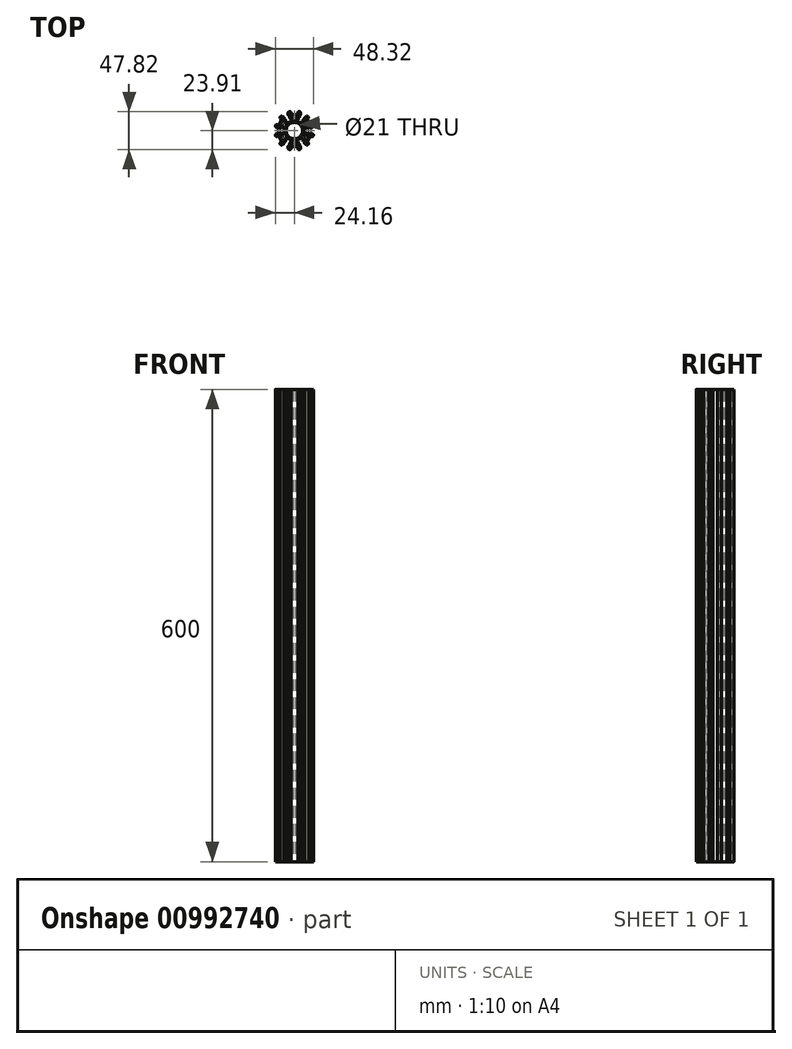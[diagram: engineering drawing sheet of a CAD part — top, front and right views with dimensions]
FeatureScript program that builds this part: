
annotation { "Feature Type Name" : "Feature", "Feature Type Description" : "" }
export const myFeature = defineFeature(function(context is Context, id is Id, definition is map)
    precondition{}
    {
        {
            var Q0;
            Q0=qCreatedBy(makeId("Top.planeOp"),FACE);
            var sketch = newSketch(context, id + "F0", { "sketchPlane" : qUnion([Q0])});
            skLineSegment(sketch, "E0.bottom", {"start": v(-8, -23.9) * mm, "end": v(-4.5, -23.9) * mm});
            skLineSegment(sketch, "E0.top", {"start": v(-8, -19.1) * mm, "end": v(-1.5, -19.1) * mm});
            skLineSegment(sketch, "E0.left", {"start": v(-8, -23.9) * mm, "end": v(-8, -19.1) * mm});
            skLineSegment(sketch, "E0.right", {"start": v(8, -23.9) * mm, "end": v(8, -19.1) * mm});
            skLineSegment(sketch, "E1.bottom", {"start": v(-6.25, -22.6) * mm, "end": v(-4.5, -22.6) * mm});
            skLineSegment(sketch, "E1.top", {"start": v(-6.25, -20.6) * mm, "end": v(6.25, -20.6) * mm});
            skLineSegment(sketch, "E1.left", {"start": v(-6.25, -22.6) * mm, "end": v(-6.25, -20.6) * mm});
            skLineSegment(sketch, "E1.right", {"start": v(6.25, -22.6) * mm, "end": v(6.25, -20.6) * mm});
            skLineSegment(sketch, "E2.left", {"start": v(-1.5, -19.1) * mm, "end": v(-1.5, -17.7) * mm});
            skLineSegment(sketch, "E2.right", {"start": v(1.5, -19.1) * mm, "end": v(1.5, -17.7) * mm});
            skArc(sketch, "E3", {"start": v(1.5, -12.4) * mm, "mid": v(6.25, -10.83) * mm, "end": v(10, -7.5) * mm});
            skLineSegment(sketch, "E4.left", {"start": v(-4.5, -23.9) * mm, "end": v(-4.5, -22.6) * mm});
            skLineSegment(sketch, "E4.right", {"start": v(4.5, -23.9) * mm, "end": v(4.5, -22.6) * mm});
            skLineSegment(sketch, "E5.trimOffspring", {"start": v(4.5, -23.9) * mm, "end": v(8, -23.9) * mm});
            skLineSegment(sketch, "E6.trimOffspring", {"start": v(4.5, -22.6) * mm, "end": v(6.25, -22.6) * mm});
            skLineSegment(sketch, "E7.trimOffspring", {"start": v(1.5, -19.1) * mm, "end": v(8, -19.1) * mm});
            skCircle(sketch, "E8", {"center": v(0, 0) * mm, "radius": 10.5 * mm});
            skLineSegment(sketch, "E9.bottom", {"start": v(-6.5, -17.7) * mm, "end": v(-1.5, -17.7) * mm});
            skLineSegment(sketch, "E9.top", {"start": v(-6.5, -16.4) * mm, "end": v(-1.5, -16.4) * mm});
            skLineSegment(sketch, "E9.left", {"start": v(-6.5, -17.7) * mm, "end": v(-6.5, -16.4) * mm});
            skLineSegment(sketch, "E9.right", {"start": v(6.5, -17.7) * mm, "end": v(6.5, -16.4) * mm});
            skLineSegment(sketch, "E10.bottom", {"start": v(-5, -15) * mm, "end": v(-1.5, -15) * mm});
            skLineSegment(sketch, "E10.top", {"start": v(-5, -13.7) * mm, "end": v(-1.5, -13.7) * mm});
            skLineSegment(sketch, "E10.left", {"start": v(-5, -15) * mm, "end": v(-5, -13.7) * mm});
            skLineSegment(sketch, "E10.right", {"start": v(5, -15) * mm, "end": v(5, -13.7) * mm});
            skLineSegment(sketch, "E11.trimOffspring", {"start": v(1.5, -17.7) * mm, "end": v(6.5, -17.7) * mm});
            skLineSegment(sketch, "E12.trimOffspring", {"start": v(-1.5, -16.4) * mm, "end": v(-1.5, -15) * mm});
            skLineSegment(sketch, "E13.trimOffspring", {"start": v(1.5, -16.4) * mm, "end": v(6.5, -16.4) * mm});
            skLineSegment(sketch, "E14.trimOffspring", {"start": v(1.5, -15) * mm, "end": v(5, -15) * mm});
            skLineSegment(sketch, "E15.trimOffspring", {"start": v(1.5, -16.4) * mm, "end": v(1.5, -15) * mm});
            skLineSegment(sketch, "E16.trimOffspring", {"start": v(1.5, -13.7) * mm, "end": v(1.5, -12.4) * mm});
            skLineSegment(sketch, "E17.trimOffspring", {"start": v(-1.5, -13.7) * mm, "end": v(-1.5, -12.4) * mm});
            skLineSegment(sketch, "E18.trimOffspring", {"start": v(1.5, -13.7) * mm, "end": v(5, -13.7) * mm});
            skLineSegment(sketch, "E19.1.0", {"start": v(16.7, -18.88) * mm, "end": v(18.46, -15.85) * mm});
            skLineSegment(sketch, "E19.1.1", {"start": v(13.75, -6.2) * mm, "end": v(15.5, -3.17) * mm});
            skLineSegment(sketch, "E19.1.2", {"start": v(12.55, -16.48) * mm, "end": v(15.8, -10.85) * mm});
            skLineSegment(sketch, "E19.1.3", {"start": v(24.7, -5.03) * mm, "end": v(20.55, -2.63) * mm});
            skLineSegment(sketch, "E19.1.4", {"start": v(10.5, -11.83) * mm, "end": v(12.25, -8.8) * mm});
            skLineSegment(sketch, "E19.1.5", {"start": v(9.37, -11.18) * mm, "end": v(11.12, -8.15) * mm});
            skLineSegment(sketch, "E19.1.6", {"start": v(16.46, -16.72) * mm, "end": v(14.72, -15.72) * mm});
            skLineSegment(sketch, "E19.1.7", {"start": v(14.96, -6.9) * mm, "end": v(17.46, -2.58) * mm});
            skLineSegment(sketch, "E19.1.8", {"start": v(12.62, -5.56) * mm, "end": v(14.37, -2.52) * mm});
            skLineSegment(sketch, "E19.1.9", {"start": v(22.96, -8.06) * mm, "end": v(24.7, -5.03) * mm});
            skLineSegment(sketch, "E19.1.10", {"start": v(14.72, -15.72) * mm, "end": v(20.97, -4.9) * mm});
            skLineSegment(sketch, "E19.1.11", {"start": v(22.7, -5.9) * mm, "end": v(20.97, -4.9) * mm});
            skLineSegment(sketch, "E19.1.12", {"start": v(16.7, -18.88) * mm, "end": v(12.55, -16.48) * mm});
            skLineSegment(sketch, "E19.1.13", {"start": v(17.3, -8.26) * mm, "end": v(20.55, -2.63) * mm});
            skLineSegment(sketch, "E19.1.14", {"start": v(12.09, -14.48) * mm, "end": v(14.59, -10.15) * mm});
            skLineSegment(sketch, "E19.1.15", {"start": v(10.96, -13.83) * mm, "end": v(13.46, -9.5) * mm});
            skLineSegment(sketch, "E19.1.16", {"start": v(16.09, -7.56) * mm, "end": v(18.59, -3.23) * mm});
            skLineSegment(sketch, "E19.1.17", {"start": v(22.96, -8.06) * mm, "end": v(21.83, -7.4) * mm});
            skLineSegment(sketch, "E19.1.18", {"start": v(13.46, -9.5) * mm, "end": v(12.25, -8.8) * mm});
            skLineSegment(sketch, "E19.1.19", {"start": v(15.5, -3.17) * mm, "end": v(14.37, -2.52) * mm});
            skLineSegment(sketch, "E19.1.20", {"start": v(21.83, -7.4) * mm, "end": v(22.7, -5.9) * mm});
            skLineSegment(sketch, "E19.1.21", {"start": v(18.46, -15.85) * mm, "end": v(17.33, -15.2) * mm});
            skLineSegment(sketch, "E19.1.22", {"start": v(10.5, -11.83) * mm, "end": v(9.37, -11.18) * mm});
            skLineSegment(sketch, "E19.1.23", {"start": v(12.09, -14.48) * mm, "end": v(10.96, -13.83) * mm});
            skLineSegment(sketch, "E19.1.24", {"start": v(15.8, -10.85) * mm, "end": v(14.59, -10.15) * mm});
            skLineSegment(sketch, "E19.1.25", {"start": v(17.3, -8.26) * mm, "end": v(16.09, -7.56) * mm});
            skLineSegment(sketch, "E19.1.26", {"start": v(16.46, -16.72) * mm, "end": v(17.33, -15.2) * mm});
            skLineSegment(sketch, "E19.1.27", {"start": v(18.59, -3.23) * mm, "end": v(17.46, -2.58) * mm});
            skLineSegment(sketch, "E19.1.28", {"start": v(14.96, -6.9) * mm, "end": v(13.75, -6.2) * mm});
            skLineSegment(sketch, "E19.1.29", {"start": v(11.12, -8.15) * mm, "end": v(10, -7.5) * mm});
            skLineSegment(sketch, "E19.1.30", {"start": v(12.62, -5.56) * mm, "end": v(11.5, -4.9) * mm});
            skLineSegment(sketch, "E19.2.0", {"start": v(24.7, 5.03) * mm, "end": v(22.96, 8.06) * mm});
            skLineSegment(sketch, "E19.2.1", {"start": v(12.25, 8.8) * mm, "end": v(10.5, 11.83) * mm});
            skLineSegment(sketch, "E19.2.2", {"start": v(20.55, 2.63) * mm, "end": v(17.3, 8.26) * mm});
            skLineSegment(sketch, "E19.2.3", {"start": v(16.7, 18.88) * mm, "end": v(12.55, 16.48) * mm});
            skLineSegment(sketch, "E19.2.4", {"start": v(15.5, 3.17) * mm, "end": v(13.75, 6.2) * mm});
            skLineSegment(sketch, "E19.2.5", {"start": v(14.37, 2.52) * mm, "end": v(12.62, 5.56) * mm});
            skLineSegment(sketch, "E19.2.6", {"start": v(22.7, 5.9) * mm, "end": v(20.97, 4.9) * mm});
            skLineSegment(sketch, "E19.2.7", {"start": v(13.46, 9.5) * mm, "end": v(10.96, 13.83) * mm});
            skLineSegment(sketch, "E19.2.8", {"start": v(11.12, 8.15) * mm, "end": v(9.37, 11.18) * mm});
            skLineSegment(sketch, "E19.2.9", {"start": v(18.46, 15.85) * mm, "end": v(16.7, 18.88) * mm});
            skLineSegment(sketch, "E19.2.10", {"start": v(20.97, 4.9) * mm, "end": v(14.72, 15.72) * mm});
            skLineSegment(sketch, "E19.2.11", {"start": v(16.46, 16.72) * mm, "end": v(14.72, 15.72) * mm});
            skLineSegment(sketch, "E19.2.12", {"start": v(24.7, 5.03) * mm, "end": v(20.55, 2.63) * mm});
            skLineSegment(sketch, "E19.2.13", {"start": v(15.8, 10.85) * mm, "end": v(12.55, 16.48) * mm});
            skLineSegment(sketch, "E19.2.14", {"start": v(18.59, 3.23) * mm, "end": v(16.09, 7.56) * mm});
            skLineSegment(sketch, "E19.2.15", {"start": v(17.46, 2.58) * mm, "end": v(14.96, 6.9) * mm});
            skLineSegment(sketch, "E19.2.16", {"start": v(14.59, 10.15) * mm, "end": v(12.09, 14.48) * mm});
            skLineSegment(sketch, "E19.2.17", {"start": v(18.46, 15.85) * mm, "end": v(17.33, 15.2) * mm});
            skLineSegment(sketch, "E19.2.18", {"start": v(14.96, 6.9) * mm, "end": v(13.75, 6.2) * mm});
            skLineSegment(sketch, "E19.2.19", {"start": v(10.5, 11.83) * mm, "end": v(9.37, 11.18) * mm});
            skLineSegment(sketch, "E19.2.20", {"start": v(17.33, 15.2) * mm, "end": v(16.46, 16.72) * mm});
            skLineSegment(sketch, "E19.2.21", {"start": v(22.96, 8.06) * mm, "end": v(21.83, 7.4) * mm});
            skLineSegment(sketch, "E19.2.22", {"start": v(15.5, 3.17) * mm, "end": v(14.37, 2.52) * mm});
            skLineSegment(sketch, "E19.2.23", {"start": v(18.59, 3.23) * mm, "end": v(17.46, 2.58) * mm});
            skLineSegment(sketch, "E19.2.24", {"start": v(17.3, 8.26) * mm, "end": v(16.09, 7.56) * mm});
            skLineSegment(sketch, "E19.2.25", {"start": v(15.8, 10.85) * mm, "end": v(14.59, 10.15) * mm});
            skLineSegment(sketch, "E19.2.26", {"start": v(22.7, 5.9) * mm, "end": v(21.83, 7.4) * mm});
            skLineSegment(sketch, "E19.2.27", {"start": v(12.09, 14.48) * mm, "end": v(10.96, 13.83) * mm});
            skLineSegment(sketch, "E19.2.28", {"start": v(13.46, 9.5) * mm, "end": v(12.25, 8.8) * mm});
            skLineSegment(sketch, "E19.2.29", {"start": v(12.62, 5.56) * mm, "end": v(11.5, 4.9) * mm});
            skLineSegment(sketch, "E19.2.30", {"start": v(11.12, 8.15) * mm, "end": v(10, 7.5) * mm});
            skLineSegment(sketch, "E19.3.0", {"start": v(8, 23.9) * mm, "end": v(4.5, 23.9) * mm});
            skLineSegment(sketch, "E19.3.1", {"start": v(-1.5, 15) * mm, "end": v(-5, 15) * mm});
            skLineSegment(sketch, "E19.3.2", {"start": v(8, 19.1) * mm, "end": v(1.5, 19.1) * mm});
            skLineSegment(sketch, "E19.3.3", {"start": v(-8, 23.9) * mm, "end": v(-8, 19.1) * mm});
            skLineSegment(sketch, "E19.3.4", {"start": v(5, 15) * mm, "end": v(1.5, 15) * mm});
            skLineSegment(sketch, "E19.3.5", {"start": v(5, 13.7) * mm, "end": v(1.5, 13.7) * mm});
            skLineSegment(sketch, "E19.3.6", {"start": v(6.25, 22.6) * mm, "end": v(6.25, 20.6) * mm});
            skLineSegment(sketch, "E19.3.7", {"start": v(-1.5, 16.4) * mm, "end": v(-6.5, 16.4) * mm});
            skLineSegment(sketch, "E19.3.8", {"start": v(-1.5, 13.7) * mm, "end": v(-5, 13.7) * mm});
            skLineSegment(sketch, "E19.3.9", {"start": v(-4.5, 23.9) * mm, "end": v(-8, 23.9) * mm});
            skLineSegment(sketch, "E19.3.10", {"start": v(6.25, 20.6) * mm, "end": v(-6.25, 20.6) * mm});
            skLineSegment(sketch, "E19.3.11", {"start": v(-6.25, 22.6) * mm, "end": v(-6.25, 20.6) * mm});
            skLineSegment(sketch, "E19.3.12", {"start": v(8, 23.9) * mm, "end": v(8, 19.1) * mm});
            skLineSegment(sketch, "E19.3.13", {"start": v(-1.5, 19.1) * mm, "end": v(-8, 19.1) * mm});
            skLineSegment(sketch, "E19.3.14", {"start": v(6.5, 17.7) * mm, "end": v(1.5, 17.7) * mm});
            skLineSegment(sketch, "E19.3.15", {"start": v(6.5, 16.4) * mm, "end": v(1.5, 16.4) * mm});
            skLineSegment(sketch, "E19.3.16", {"start": v(-1.5, 17.7) * mm, "end": v(-6.5, 17.7) * mm});
            skLineSegment(sketch, "E19.3.17", {"start": v(-4.5, 23.9) * mm, "end": v(-4.5, 22.6) * mm});
            skLineSegment(sketch, "E19.3.18", {"start": v(1.5, 16.4) * mm, "end": v(1.5, 15) * mm});
            skLineSegment(sketch, "E19.3.19", {"start": v(-5, 15) * mm, "end": v(-5, 13.7) * mm});
            skLineSegment(sketch, "E19.3.20", {"start": v(-4.5, 22.6) * mm, "end": v(-6.25, 22.6) * mm});
            skLineSegment(sketch, "E19.3.21", {"start": v(4.5, 23.9) * mm, "end": v(4.5, 22.6) * mm});
            skLineSegment(sketch, "E19.3.22", {"start": v(5, 15) * mm, "end": v(5, 13.7) * mm});
            skLineSegment(sketch, "E19.3.23", {"start": v(6.5, 17.7) * mm, "end": v(6.5, 16.4) * mm});
            skLineSegment(sketch, "E19.3.24", {"start": v(1.5, 19.1) * mm, "end": v(1.5, 17.7) * mm});
            skLineSegment(sketch, "E19.3.25", {"start": v(-1.5, 19.1) * mm, "end": v(-1.5, 17.7) * mm});
            skLineSegment(sketch, "E19.3.26", {"start": v(6.25, 22.6) * mm, "end": v(4.5, 22.6) * mm});
            skLineSegment(sketch, "E19.3.27", {"start": v(-6.5, 17.7) * mm, "end": v(-6.5, 16.4) * mm});
            skLineSegment(sketch, "E19.3.28", {"start": v(-1.5, 16.4) * mm, "end": v(-1.5, 15) * mm});
            skLineSegment(sketch, "E19.3.29", {"start": v(1.5, 13.7) * mm, "end": v(1.5, 12.4) * mm});
            skLineSegment(sketch, "E19.3.30", {"start": v(-1.5, 13.7) * mm, "end": v(-1.5, 12.4) * mm});
            skLineSegment(sketch, "E19.4.0", {"start": v(-16.7, 18.88) * mm, "end": v(-18.46, 15.85) * mm});
            skLineSegment(sketch, "E19.4.1", {"start": v(-13.75, 6.2) * mm, "end": v(-15.5, 3.17) * mm});
            skLineSegment(sketch, "E19.4.2", {"start": v(-12.55, 16.48) * mm, "end": v(-15.8, 10.85) * mm});
            skLineSegment(sketch, "E19.4.3", {"start": v(-24.7, 5.03) * mm, "end": v(-20.55, 2.63) * mm});
            skLineSegment(sketch, "E19.4.4", {"start": v(-10.5, 11.83) * mm, "end": v(-12.25, 8.8) * mm});
            skLineSegment(sketch, "E19.4.5", {"start": v(-9.37, 11.18) * mm, "end": v(-11.12, 8.15) * mm});
            skLineSegment(sketch, "E19.4.6", {"start": v(-16.46, 16.72) * mm, "end": v(-14.72, 15.72) * mm});
            skLineSegment(sketch, "E19.4.7", {"start": v(-14.96, 6.9) * mm, "end": v(-17.46, 2.58) * mm});
            skLineSegment(sketch, "E19.4.8", {"start": v(-12.62, 5.56) * mm, "end": v(-14.37, 2.52) * mm});
            skLineSegment(sketch, "E19.4.9", {"start": v(-22.96, 8.06) * mm, "end": v(-24.7, 5.03) * mm});
            skLineSegment(sketch, "E19.4.10", {"start": v(-14.72, 15.72) * mm, "end": v(-20.97, 4.9) * mm});
            skLineSegment(sketch, "E19.4.11", {"start": v(-22.7, 5.9) * mm, "end": v(-20.97, 4.9) * mm});
            skLineSegment(sketch, "E19.4.12", {"start": v(-16.7, 18.88) * mm, "end": v(-12.55, 16.48) * mm});
            skLineSegment(sketch, "E19.4.13", {"start": v(-17.3, 8.26) * mm, "end": v(-20.55, 2.63) * mm});
            skLineSegment(sketch, "E19.4.14", {"start": v(-12.09, 14.48) * mm, "end": v(-14.59, 10.15) * mm});
            skLineSegment(sketch, "E19.4.15", {"start": v(-10.96, 13.83) * mm, "end": v(-13.46, 9.5) * mm});
            skLineSegment(sketch, "E19.4.16", {"start": v(-16.09, 7.56) * mm, "end": v(-18.59, 3.23) * mm});
            skLineSegment(sketch, "E19.4.17", {"start": v(-22.96, 8.06) * mm, "end": v(-21.83, 7.4) * mm});
            skLineSegment(sketch, "E19.4.18", {"start": v(-13.46, 9.5) * mm, "end": v(-12.25, 8.8) * mm});
            skLineSegment(sketch, "E19.4.19", {"start": v(-15.5, 3.17) * mm, "end": v(-14.37, 2.52) * mm});
            skLineSegment(sketch, "E19.4.20", {"start": v(-21.83, 7.4) * mm, "end": v(-22.7, 5.9) * mm});
            skLineSegment(sketch, "E19.4.21", {"start": v(-18.46, 15.85) * mm, "end": v(-17.33, 15.2) * mm});
            skLineSegment(sketch, "E19.4.22", {"start": v(-10.5, 11.83) * mm, "end": v(-9.37, 11.18) * mm});
            skLineSegment(sketch, "E19.4.23", {"start": v(-12.09, 14.48) * mm, "end": v(-10.96, 13.83) * mm});
            skLineSegment(sketch, "E19.4.24", {"start": v(-15.8, 10.85) * mm, "end": v(-14.59, 10.15) * mm});
            skLineSegment(sketch, "E19.4.25", {"start": v(-17.3, 8.26) * mm, "end": v(-16.09, 7.56) * mm});
            skLineSegment(sketch, "E19.4.26", {"start": v(-16.46, 16.72) * mm, "end": v(-17.33, 15.2) * mm});
            skLineSegment(sketch, "E19.4.27", {"start": v(-18.59, 3.23) * mm, "end": v(-17.46, 2.58) * mm});
            skLineSegment(sketch, "E19.4.28", {"start": v(-14.96, 6.9) * mm, "end": v(-13.75, 6.2) * mm});
            skLineSegment(sketch, "E19.4.29", {"start": v(-11.12, 8.15) * mm, "end": v(-10, 7.5) * mm});
            skLineSegment(sketch, "E19.4.30", {"start": v(-12.62, 5.56) * mm, "end": v(-11.5, 4.9) * mm});
            skLineSegment(sketch, "E19.5.0", {"start": v(-24.7, -5.03) * mm, "end": v(-22.96, -8.06) * mm});
            skLineSegment(sketch, "E19.5.1", {"start": v(-12.25, -8.8) * mm, "end": v(-10.5, -11.83) * mm});
            skLineSegment(sketch, "E19.5.2", {"start": v(-20.55, -2.63) * mm, "end": v(-17.3, -8.26) * mm});
            skLineSegment(sketch, "E19.5.3", {"start": v(-16.7, -18.88) * mm, "end": v(-12.55, -16.48) * mm});
            skLineSegment(sketch, "E19.5.4", {"start": v(-15.5, -3.17) * mm, "end": v(-13.75, -6.2) * mm});
            skLineSegment(sketch, "E19.5.5", {"start": v(-14.37, -2.52) * mm, "end": v(-12.62, -5.56) * mm});
            skLineSegment(sketch, "E19.5.6", {"start": v(-22.7, -5.9) * mm, "end": v(-20.97, -4.9) * mm});
            skLineSegment(sketch, "E19.5.7", {"start": v(-13.46, -9.5) * mm, "end": v(-10.96, -13.83) * mm});
            skLineSegment(sketch, "E19.5.8", {"start": v(-11.12, -8.15) * mm, "end": v(-9.37, -11.18) * mm});
            skLineSegment(sketch, "E19.5.9", {"start": v(-18.46, -15.85) * mm, "end": v(-16.7, -18.88) * mm});
            skLineSegment(sketch, "E19.5.10", {"start": v(-20.97, -4.9) * mm, "end": v(-14.72, -15.72) * mm});
            skLineSegment(sketch, "E19.5.11", {"start": v(-16.46, -16.72) * mm, "end": v(-14.72, -15.72) * mm});
            skLineSegment(sketch, "E19.5.12", {"start": v(-24.7, -5.03) * mm, "end": v(-20.55, -2.63) * mm});
            skLineSegment(sketch, "E19.5.13", {"start": v(-15.8, -10.85) * mm, "end": v(-12.55, -16.48) * mm});
            skLineSegment(sketch, "E19.5.14", {"start": v(-18.59, -3.23) * mm, "end": v(-16.09, -7.56) * mm});
            skLineSegment(sketch, "E19.5.15", {"start": v(-17.46, -2.58) * mm, "end": v(-14.96, -6.9) * mm});
            skLineSegment(sketch, "E19.5.16", {"start": v(-14.59, -10.15) * mm, "end": v(-12.09, -14.48) * mm});
            skLineSegment(sketch, "E19.5.17", {"start": v(-18.46, -15.85) * mm, "end": v(-17.33, -15.2) * mm});
            skLineSegment(sketch, "E19.5.18", {"start": v(-14.96, -6.9) * mm, "end": v(-13.75, -6.2) * mm});
            skLineSegment(sketch, "E19.5.19", {"start": v(-10.5, -11.83) * mm, "end": v(-9.37, -11.18) * mm});
            skLineSegment(sketch, "E19.5.20", {"start": v(-17.33, -15.2) * mm, "end": v(-16.46, -16.72) * mm});
            skLineSegment(sketch, "E19.5.21", {"start": v(-22.96, -8.06) * mm, "end": v(-21.83, -7.4) * mm});
            skLineSegment(sketch, "E19.5.22", {"start": v(-15.5, -3.17) * mm, "end": v(-14.37, -2.52) * mm});
            skLineSegment(sketch, "E19.5.23", {"start": v(-18.59, -3.23) * mm, "end": v(-17.46, -2.58) * mm});
            skLineSegment(sketch, "E19.5.24", {"start": v(-17.3, -8.26) * mm, "end": v(-16.09, -7.56) * mm});
            skLineSegment(sketch, "E19.5.25", {"start": v(-15.8, -10.85) * mm, "end": v(-14.59, -10.15) * mm});
            skLineSegment(sketch, "E19.5.26", {"start": v(-22.7, -5.9) * mm, "end": v(-21.83, -7.4) * mm});
            skLineSegment(sketch, "E19.5.27", {"start": v(-12.09, -14.48) * mm, "end": v(-10.96, -13.83) * mm});
            skLineSegment(sketch, "E19.5.28", {"start": v(-13.46, -9.5) * mm, "end": v(-12.25, -8.8) * mm});
            skLineSegment(sketch, "E19.5.29", {"start": v(-12.62, -5.56) * mm, "end": v(-11.5, -4.9) * mm});
            skLineSegment(sketch, "E19.5.30", {"start": v(-11.12, -8.15) * mm, "end": v(-10, -7.5) * mm});
            skArc(sketch, "E20.trimOffspring", {"start": v(-10, -7.5) * mm, "mid": v(-6.25, -10.83) * mm, "end": v(-1.5, -12.4) * mm});
            skArc(sketch, "E21.trimOffspring", {"start": v(-11.5, 4.9) * mm, "mid": v(-12.5, 0) * mm, "end": v(-11.5, -4.9) * mm});
            skArc(sketch, "E22.trimOffspring", {"start": v(11.5, -4.9) * mm, "mid": v(12.5, 0) * mm, "end": v(11.5, 4.9) * mm});
            skArc(sketch, "E23.trimOffspring", {"start": v(-1.5, 12.4) * mm, "mid": v(-6.25, 10.83) * mm, "end": v(-10, 7.5) * mm});
            skArc(sketch, "E24.trimOffspring", {"start": v(10, 7.5) * mm, "mid": v(6.25, 10.83) * mm, "end": v(1.5, 12.4) * mm});
            skSolve(sketch);
        }
        {
            var Q0;
            Q0 = qSketchRegion(id + "F0", true);
            extrude(context, id + "F1", {"entities" : qUnion([Q0]), "depth" : 600 * mm, "offsetDistance" : 25 * mm});
        }
        {
            var Q0;
            Q0=makeQuery(id+"F1.opExtrude","SWEPT_EDGE",EDGE,{"disambiguationData":[OSD([sQuery(id+"F0.wireOp",EDGE,"E19.3.3"),sQuery(id+"F0.wireOp",EDGE,"E19.3.9")])]});
            var Q1;
            Q1=makeQuery(id+"F1.opExtrude","SWEPT_EDGE",EDGE,{"disambiguationData":[OSD([sQuery(id+"F0.wireOp",EDGE,"E19.3.0"),sQuery(id+"F0.wireOp",EDGE,"E19.3.12")])]});
            var Q2;
            Q2=makeQuery(id+"F1.opExtrude","SWEPT_EDGE",EDGE,{"disambiguationData":[OSD([sQuery(id+"F0.wireOp",EDGE,"E19.3.2"),sQuery(id+"F0.wireOp",EDGE,"E19.3.12")])]});
            var Q3;
            Q3=makeQuery(id+"F1.opExtrude","SWEPT_EDGE",EDGE,{"disambiguationData":[OSD([sQuery(id+"F0.wireOp",EDGE,"E19.3.3"),sQuery(id+"F0.wireOp",EDGE,"E19.3.13")])]});
            var Q4;
            Q4=makeQuery(id+"F1.opExtrude","SWEPT_EDGE",EDGE,{"disambiguationData":[OSD([sQuery(id+"F0.wireOp",EDGE,"E19.2.3"),sQuery(id+"F0.wireOp",EDGE,"E19.2.13")])]});
            var Q5;
            Q5=makeQuery(id+"F1.opExtrude","SWEPT_EDGE",EDGE,{"disambiguationData":[OSD([sQuery(id+"F0.wireOp",EDGE,"E19.2.2"),sQuery(id+"F0.wireOp",EDGE,"E19.2.12")])]});
            var Q6;
            Q6=makeQuery(id+"F1.opExtrude","SWEPT_EDGE",EDGE,{"disambiguationData":[OSD([sQuery(id+"F0.wireOp",EDGE,"E19.2.0"),sQuery(id+"F0.wireOp",EDGE,"E19.2.12")])]});
            var Q7;
            Q7=makeQuery(id+"F1.opExtrude","SWEPT_EDGE",EDGE,{"disambiguationData":[OSD([sQuery(id+"F0.wireOp",EDGE,"E19.2.3"),sQuery(id+"F0.wireOp",EDGE,"E19.2.9")])]});
            var Q8;
            Q8=makeQuery(id+"F1.opExtrude","SWEPT_EDGE",EDGE,{"disambiguationData":[OSD([sQuery(id+"F0.wireOp",EDGE,"E19.1.3"),sQuery(id+"F0.wireOp",EDGE,"E19.1.13")])]});
            var Q9;
            Q9=makeQuery(id+"F1.opExtrude","SWEPT_EDGE",EDGE,{"disambiguationData":[OSD([sQuery(id+"F0.wireOp",EDGE,"E19.1.3"),sQuery(id+"F0.wireOp",EDGE,"E19.1.9")])]});
            var Q10;
            Q10=makeQuery(id+"F1.opExtrude","SWEPT_EDGE",EDGE,{"disambiguationData":[OSD([sQuery(id+"F0.wireOp",EDGE,"E19.1.2"),sQuery(id+"F0.wireOp",EDGE,"E19.1.12")])]});
            var Q11;
            Q11=makeQuery(id+"F1.opExtrude","SWEPT_EDGE",EDGE,{"disambiguationData":[OSD([sQuery(id+"F0.wireOp",EDGE,"E19.1.0"),sQuery(id+"F0.wireOp",EDGE,"E19.1.12")])]});
            var Q12;
            Q12=makeQuery(id+"F1.opExtrude","SWEPT_EDGE",EDGE,{"disambiguationData":[OSD([sQuery(id+"F0.wireOp",EDGE,"E0.right"),sQuery(id+"F0.wireOp",EDGE,"E5.trimOffspring")])]});
            var Q13;
            Q13=makeQuery(id+"F1.opExtrude","SWEPT_EDGE",EDGE,{"disambiguationData":[OSD([sQuery(id+"F0.wireOp",EDGE,"E0.right"),sQuery(id+"F0.wireOp",EDGE,"E7.trimOffspring")])]});
            var Q14;
            Q14=makeQuery(id+"F1.opExtrude","SWEPT_EDGE",EDGE,{"disambiguationData":[OSD([sQuery(id+"F0.wireOp",EDGE,"E0.top"),sQuery(id+"F0.wireOp",EDGE,"E0.left")])]});
            var Q15;
            Q15=makeQuery(id+"F1.opExtrude","SWEPT_EDGE",EDGE,{"disambiguationData":[OSD([sQuery(id+"F0.wireOp",EDGE,"E0.bottom"),sQuery(id+"F0.wireOp",EDGE,"E0.left")])]});
            var Q16;
            Q16=makeQuery(id+"F1.opExtrude","SWEPT_EDGE",EDGE,{"disambiguationData":[OSD([sQuery(id+"F0.wireOp",EDGE,"E19.5.3"),sQuery(id+"F0.wireOp",EDGE,"E19.5.13")])]});
            var Q17;
            Q17=makeQuery(id+"F1.opExtrude","SWEPT_EDGE",EDGE,{"disambiguationData":[OSD([sQuery(id+"F0.wireOp",EDGE,"E19.5.3"),sQuery(id+"F0.wireOp",EDGE,"E19.5.9")])]});
            var Q18;
            Q18=makeQuery(id+"F1.opExtrude","SWEPT_EDGE",EDGE,{"disambiguationData":[OSD([sQuery(id+"F0.wireOp",EDGE,"E19.5.2"),sQuery(id+"F0.wireOp",EDGE,"E19.5.12")])]});
            var Q19;
            Q19=makeQuery(id+"F1.opExtrude","SWEPT_EDGE",EDGE,{"disambiguationData":[OSD([sQuery(id+"F0.wireOp",EDGE,"E19.5.0"),sQuery(id+"F0.wireOp",EDGE,"E19.5.12")])]});
            var Q20;
            Q20=makeQuery(id+"F1.opExtrude","SWEPT_EDGE",EDGE,{"disambiguationData":[OSD([sQuery(id+"F0.wireOp",EDGE,"E19.4.3"),sQuery(id+"F0.wireOp",EDGE,"E19.4.13")])]});
            var Q21;
            Q21=makeQuery(id+"F1.opExtrude","SWEPT_EDGE",EDGE,{"disambiguationData":[OSD([sQuery(id+"F0.wireOp",EDGE,"E19.4.3"),sQuery(id+"F0.wireOp",EDGE,"E19.4.9")])]});
            var Q22;
            Q22=makeQuery(id+"F1.opExtrude","SWEPT_EDGE",EDGE,{"disambiguationData":[OSD([sQuery(id+"F0.wireOp",EDGE,"E19.4.2"),sQuery(id+"F0.wireOp",EDGE,"E19.4.12")])]});
            var Q23;
            Q23=makeQuery(id+"F1.opExtrude","SWEPT_EDGE",EDGE,{"disambiguationData":[OSD([sQuery(id+"F0.wireOp",EDGE,"E19.4.0"),sQuery(id+"F0.wireOp",EDGE,"E19.4.12")])]});
            fillet(context, id + "F2", {"entities" : qUnion([Q0, Q1, Q2, Q3, Q4, Q5, Q6, Q7, Q8, Q9, Q10, Q11, Q12, Q13, Q14, Q15, Q16, Q17, Q18, Q19, Q20, Q21, Q22, Q23]), "tangentPropagation" : true, "radius" : 1.5 * mm, "defaultsChanged" : false, "vertexSettings" : [], "allowEdgeOverflow" : false});
        }
        {
            var Q0;
            Q0=makeQuery(id+"F1.opExtrude","SWEPT_EDGE",EDGE,{"disambiguationData":[OSD([sQuery(id+"F0.wireOp",EDGE,"E19.3.0"),sQuery(id+"F0.wireOp",EDGE,"E19.3.21")])]});
            var Q1;
            Q1=makeQuery(id+"F1.opExtrude","SWEPT_EDGE",EDGE,{"disambiguationData":[OSD([sQuery(id+"F0.wireOp",EDGE,"E19.3.9"),sQuery(id+"F0.wireOp",EDGE,"E19.3.17")])]});
            var Q2;
            Q2=makeQuery(id+"F1.opExtrude","SWEPT_EDGE",EDGE,{"disambiguationData":[OSD([sQuery(id+"F0.wireOp",EDGE,"E19.3.16"),sQuery(id+"F0.wireOp",EDGE,"E19.3.27")])]});
            var Q3;
            Q3=makeQuery(id+"F1.opExtrude","SWEPT_EDGE",EDGE,{"disambiguationData":[OSD([sQuery(id+"F0.wireOp",EDGE,"E19.3.7"),sQuery(id+"F0.wireOp",EDGE,"E19.3.27")])]});
            var Q4;
            Q4=makeQuery(id+"F1.opExtrude","SWEPT_EDGE",EDGE,{"disambiguationData":[OSD([sQuery(id+"F0.wireOp",EDGE,"E19.3.1"),sQuery(id+"F0.wireOp",EDGE,"E19.3.19")])]});
            var Q5;
            Q5=makeQuery(id+"F1.opExtrude","SWEPT_EDGE",EDGE,{"disambiguationData":[OSD([sQuery(id+"F0.wireOp",EDGE,"E19.3.8"),sQuery(id+"F0.wireOp",EDGE,"E19.3.19")])]});
            var Q6;
            Q6=makeQuery(id+"F1.opExtrude","SWEPT_EDGE",EDGE,{"disambiguationData":[OSD([sQuery(id+"F0.wireOp",EDGE,"E19.3.14"),sQuery(id+"F0.wireOp",EDGE,"E19.3.23")])]});
            var Q7;
            Q7=makeQuery(id+"F1.opExtrude","SWEPT_EDGE",EDGE,{"disambiguationData":[OSD([sQuery(id+"F0.wireOp",EDGE,"E19.3.15"),sQuery(id+"F0.wireOp",EDGE,"E19.3.23")])]});
            var Q8;
            Q8=makeQuery(id+"F1.opExtrude","SWEPT_EDGE",EDGE,{"disambiguationData":[OSD([sQuery(id+"F0.wireOp",EDGE,"E19.3.4"),sQuery(id+"F0.wireOp",EDGE,"E19.3.22")])]});
            var Q9;
            Q9=makeQuery(id+"F1.opExtrude","SWEPT_EDGE",EDGE,{"disambiguationData":[OSD([sQuery(id+"F0.wireOp",EDGE,"E19.3.5"),sQuery(id+"F0.wireOp",EDGE,"E19.3.22")])]});
            var Q10;
            Q10=makeQuery(id+"F1.opExtrude","SWEPT_EDGE",EDGE,{"disambiguationData":[OSD([sQuery(id+"F0.wireOp",EDGE,"E19.4.0"),sQuery(id+"F0.wireOp",EDGE,"E19.4.21")])]});
            var Q11;
            Q11=makeQuery(id+"F1.opExtrude","SWEPT_EDGE",EDGE,{"disambiguationData":[OSD([sQuery(id+"F0.wireOp",EDGE,"E19.4.9"),sQuery(id+"F0.wireOp",EDGE,"E19.4.17")])]});
            var Q12;
            Q12=makeQuery(id+"F1.opExtrude","SWEPT_EDGE",EDGE,{"disambiguationData":[OSD([sQuery(id+"F0.wireOp",EDGE,"E19.4.16"),sQuery(id+"F0.wireOp",EDGE,"E19.4.27")])]});
            var Q13;
            Q13=makeQuery(id+"F1.opExtrude","SWEPT_EDGE",EDGE,{"disambiguationData":[OSD([sQuery(id+"F0.wireOp",EDGE,"E19.4.7"),sQuery(id+"F0.wireOp",EDGE,"E19.4.27")])]});
            var Q14;
            Q14=makeQuery(id+"F1.opExtrude","SWEPT_EDGE",EDGE,{"disambiguationData":[OSD([sQuery(id+"F0.wireOp",EDGE,"E19.4.1"),sQuery(id+"F0.wireOp",EDGE,"E19.4.19")])]});
            var Q15;
            Q15=makeQuery(id+"F1.opExtrude","SWEPT_EDGE",EDGE,{"disambiguationData":[OSD([sQuery(id+"F0.wireOp",EDGE,"E19.4.8"),sQuery(id+"F0.wireOp",EDGE,"E19.4.19")])]});
            var Q16;
            Q16=makeQuery(id+"F1.opExtrude","SWEPT_EDGE",EDGE,{"disambiguationData":[OSD([sQuery(id+"F0.wireOp",EDGE,"E19.4.4"),sQuery(id+"F0.wireOp",EDGE,"E19.4.22")])]});
            var Q17;
            Q17=makeQuery(id+"F1.opExtrude","SWEPT_EDGE",EDGE,{"disambiguationData":[OSD([sQuery(id+"F0.wireOp",EDGE,"E19.4.14"),sQuery(id+"F0.wireOp",EDGE,"E19.4.23")])]});
            var Q18;
            Q18=makeQuery(id+"F1.opExtrude","SWEPT_EDGE",EDGE,{"disambiguationData":[OSD([sQuery(id+"F0.wireOp",EDGE,"E19.4.15"),sQuery(id+"F0.wireOp",EDGE,"E19.4.23")])]});
            var Q19;
            Q19=makeQuery(id+"F1.opExtrude","SWEPT_EDGE",EDGE,{"disambiguationData":[OSD([sQuery(id+"F0.wireOp",EDGE,"E19.4.5"),sQuery(id+"F0.wireOp",EDGE,"E19.4.22")])]});
            var Q20;
            Q20=makeQuery(id+"F1.opExtrude","SWEPT_EDGE",EDGE,{"disambiguationData":[OSD([sQuery(id+"F0.wireOp",EDGE,"E19.5.0"),sQuery(id+"F0.wireOp",EDGE,"E19.5.21")])]});
            var Q21;
            Q21=makeQuery(id+"F1.opExtrude","SWEPT_EDGE",EDGE,{"disambiguationData":[OSD([sQuery(id+"F0.wireOp",EDGE,"E19.5.14"),sQuery(id+"F0.wireOp",EDGE,"E19.5.23")])]});
            var Q22;
            Q22=makeQuery(id+"F1.opExtrude","SWEPT_EDGE",EDGE,{"disambiguationData":[OSD([sQuery(id+"F0.wireOp",EDGE,"E19.5.15"),sQuery(id+"F0.wireOp",EDGE,"E19.5.23")])]});
            var Q23;
            Q23=makeQuery(id+"F1.opExtrude","SWEPT_EDGE",EDGE,{"disambiguationData":[OSD([sQuery(id+"F0.wireOp",EDGE,"E19.5.4"),sQuery(id+"F0.wireOp",EDGE,"E19.5.22")])]});
            var Q24;
            Q24=makeQuery(id+"F1.opExtrude","SWEPT_EDGE",EDGE,{"disambiguationData":[OSD([sQuery(id+"F0.wireOp",EDGE,"E19.5.5"),sQuery(id+"F0.wireOp",EDGE,"E19.5.22")])]});
            var Q25;
            Q25=makeQuery(id+"F1.opExtrude","SWEPT_EDGE",EDGE,{"disambiguationData":[OSD([sQuery(id+"F0.wireOp",EDGE,"E19.5.1"),sQuery(id+"F0.wireOp",EDGE,"E19.5.19")])]});
            var Q26;
            Q26=makeQuery(id+"F1.opExtrude","SWEPT_EDGE",EDGE,{"disambiguationData":[OSD([sQuery(id+"F0.wireOp",EDGE,"E19.5.8"),sQuery(id+"F0.wireOp",EDGE,"E19.5.19")])]});
            var Q27;
            Q27=makeQuery(id+"F1.opExtrude","SWEPT_EDGE",EDGE,{"disambiguationData":[OSD([sQuery(id+"F0.wireOp",EDGE,"E19.5.7"),sQuery(id+"F0.wireOp",EDGE,"E19.5.27")])]});
            var Q28;
            Q28=makeQuery(id+"F1.opExtrude","SWEPT_EDGE",EDGE,{"disambiguationData":[OSD([sQuery(id+"F0.wireOp",EDGE,"E19.5.16"),sQuery(id+"F0.wireOp",EDGE,"E19.5.27")])]});
            var Q29;
            Q29=makeQuery(id+"F1.opExtrude","SWEPT_EDGE",EDGE,{"disambiguationData":[OSD([sQuery(id+"F0.wireOp",EDGE,"E19.5.9"),sQuery(id+"F0.wireOp",EDGE,"E19.5.17")])]});
            var Q30;
            Q30=makeQuery(id+"F1.opExtrude","SWEPT_EDGE",EDGE,{"disambiguationData":[OSD([sQuery(id+"F0.wireOp",EDGE,"E9.bottom"),sQuery(id+"F0.wireOp",EDGE,"E9.left")])]});
            var Q31;
            Q31=makeQuery(id+"F1.opExtrude","SWEPT_EDGE",EDGE,{"disambiguationData":[OSD([sQuery(id+"F0.wireOp",EDGE,"E9.top"),sQuery(id+"F0.wireOp",EDGE,"E9.left")])]});
            var Q32;
            Q32=makeQuery(id+"F1.opExtrude","SWEPT_EDGE",EDGE,{"disambiguationData":[OSD([sQuery(id+"F0.wireOp",EDGE,"E10.bottom"),sQuery(id+"F0.wireOp",EDGE,"E10.left")])]});
            var Q33;
            Q33=makeQuery(id+"F1.opExtrude","SWEPT_EDGE",EDGE,{"disambiguationData":[OSD([sQuery(id+"F0.wireOp",EDGE,"E10.top"),sQuery(id+"F0.wireOp",EDGE,"E10.left")])]});
            var Q34;
            Q34=makeQuery(id+"F1.opExtrude","SWEPT_EDGE",EDGE,{"disambiguationData":[OSD([sQuery(id+"F0.wireOp",EDGE,"E0.bottom"),sQuery(id+"F0.wireOp",EDGE,"E4.left")])]});
            var Q35;
            Q35=makeQuery(id+"F1.opExtrude","SWEPT_EDGE",EDGE,{"disambiguationData":[OSD([sQuery(id+"F0.wireOp",EDGE,"E4.right"),sQuery(id+"F0.wireOp",EDGE,"E5.trimOffspring")])]});
            var Q36;
            Q36=makeQuery(id+"F1.opExtrude","SWEPT_EDGE",EDGE,{"disambiguationData":[OSD([sQuery(id+"F0.wireOp",EDGE,"E9.right"),sQuery(id+"F0.wireOp",EDGE,"E11.trimOffspring")])]});
            var Q37;
            Q37=makeQuery(id+"F1.opExtrude","SWEPT_EDGE",EDGE,{"disambiguationData":[OSD([sQuery(id+"F0.wireOp",EDGE,"E9.right"),sQuery(id+"F0.wireOp",EDGE,"E13.trimOffspring")])]});
            var Q38;
            Q38=makeQuery(id+"F1.opExtrude","SWEPT_EDGE",EDGE,{"disambiguationData":[OSD([sQuery(id+"F0.wireOp",EDGE,"E10.right"),sQuery(id+"F0.wireOp",EDGE,"E14.trimOffspring")])]});
            var Q39;
            Q39=makeQuery(id+"F1.opExtrude","SWEPT_EDGE",EDGE,{"disambiguationData":[OSD([sQuery(id+"F0.wireOp",EDGE,"E10.right"),sQuery(id+"F0.wireOp",EDGE,"E18.trimOffspring")])]});
            var Q40;
            Q40=makeQuery(id+"F1.opExtrude","SWEPT_EDGE",EDGE,{"disambiguationData":[OSD([sQuery(id+"F0.wireOp",EDGE,"E19.1.14"),sQuery(id+"F0.wireOp",EDGE,"E19.1.23")])]});
            var Q41;
            Q41=makeQuery(id+"F1.opExtrude","SWEPT_EDGE",EDGE,{"disambiguationData":[OSD([sQuery(id+"F0.wireOp",EDGE,"E19.1.15"),sQuery(id+"F0.wireOp",EDGE,"E19.1.23")])]});
            var Q42;
            Q42=makeQuery(id+"F1.opExtrude","SWEPT_EDGE",EDGE,{"disambiguationData":[OSD([sQuery(id+"F0.wireOp",EDGE,"E19.1.5"),sQuery(id+"F0.wireOp",EDGE,"E19.1.22")])]});
            var Q43;
            Q43=makeQuery(id+"F1.opExtrude","SWEPT_EDGE",EDGE,{"disambiguationData":[OSD([sQuery(id+"F0.wireOp",EDGE,"E19.1.4"),sQuery(id+"F0.wireOp",EDGE,"E19.1.22")])]});
            var Q44;
            Q44=makeQuery(id+"F1.opExtrude","SWEPT_EDGE",EDGE,{"disambiguationData":[OSD([sQuery(id+"F0.wireOp",EDGE,"E19.1.0"),sQuery(id+"F0.wireOp",EDGE,"E19.1.21")])]});
            var Q45;
            Q45=makeQuery(id+"F1.opExtrude","SWEPT_EDGE",EDGE,{"disambiguationData":[OSD([sQuery(id+"F0.wireOp",EDGE,"E19.1.9"),sQuery(id+"F0.wireOp",EDGE,"E19.1.17")])]});
            var Q46;
            Q46=makeQuery(id+"F1.opExtrude","SWEPT_EDGE",EDGE,{"disambiguationData":[OSD([sQuery(id+"F0.wireOp",EDGE,"E19.1.16"),sQuery(id+"F0.wireOp",EDGE,"E19.1.27")])]});
            var Q47;
            Q47=makeQuery(id+"F1.opExtrude","SWEPT_EDGE",EDGE,{"disambiguationData":[OSD([sQuery(id+"F0.wireOp",EDGE,"E19.1.1"),sQuery(id+"F0.wireOp",EDGE,"E19.1.19")])]});
            var Q48;
            Q48=makeQuery(id+"F1.opExtrude","SWEPT_EDGE",EDGE,{"disambiguationData":[OSD([sQuery(id+"F0.wireOp",EDGE,"E19.1.7"),sQuery(id+"F0.wireOp",EDGE,"E19.1.27")])]});
            var Q49;
            Q49=makeQuery(id+"F1.opExtrude","SWEPT_EDGE",EDGE,{"disambiguationData":[OSD([sQuery(id+"F0.wireOp",EDGE,"E19.1.8"),sQuery(id+"F0.wireOp",EDGE,"E19.1.19")])]});
            var Q50;
            Q50=makeQuery(id+"F1.opExtrude","SWEPT_EDGE",EDGE,{"disambiguationData":[OSD([sQuery(id+"F0.wireOp",EDGE,"E19.2.15"),sQuery(id+"F0.wireOp",EDGE,"E19.2.23")])]});
            var Q51;
            Q51=makeQuery(id+"F1.opExtrude","SWEPT_EDGE",EDGE,{"disambiguationData":[OSD([sQuery(id+"F0.wireOp",EDGE,"E19.2.14"),sQuery(id+"F0.wireOp",EDGE,"E19.2.23")])]});
            var Q52;
            Q52=makeQuery(id+"F1.opExtrude","SWEPT_EDGE",EDGE,{"disambiguationData":[OSD([sQuery(id+"F0.wireOp",EDGE,"E19.2.4"),sQuery(id+"F0.wireOp",EDGE,"E19.2.22")])]});
            var Q53;
            Q53=makeQuery(id+"F1.opExtrude","SWEPT_EDGE",EDGE,{"disambiguationData":[OSD([sQuery(id+"F0.wireOp",EDGE,"E19.2.5"),sQuery(id+"F0.wireOp",EDGE,"E19.2.22")])]});
            var Q54;
            Q54=makeQuery(id+"F1.opExtrude","SWEPT_EDGE",EDGE,{"disambiguationData":[OSD([sQuery(id+"F0.wireOp",EDGE,"E19.2.8"),sQuery(id+"F0.wireOp",EDGE,"E19.2.19")])]});
            var Q55;
            Q55=makeQuery(id+"F1.opExtrude","SWEPT_EDGE",EDGE,{"disambiguationData":[OSD([sQuery(id+"F0.wireOp",EDGE,"E19.2.7"),sQuery(id+"F0.wireOp",EDGE,"E19.2.27")])]});
            var Q56;
            Q56=makeQuery(id+"F1.opExtrude","SWEPT_EDGE",EDGE,{"disambiguationData":[OSD([sQuery(id+"F0.wireOp",EDGE,"E19.2.9"),sQuery(id+"F0.wireOp",EDGE,"E19.2.17")])]});
            var Q57;
            Q57=makeQuery(id+"F1.opExtrude","SWEPT_EDGE",EDGE,{"disambiguationData":[OSD([sQuery(id+"F0.wireOp",EDGE,"E19.2.0"),sQuery(id+"F0.wireOp",EDGE,"E19.2.21")])]});
            var Q58;
            Q58=makeQuery(id+"F1.opExtrude","SWEPT_EDGE",EDGE,{"disambiguationData":[OSD([sQuery(id+"F0.wireOp",EDGE,"E19.2.16"),sQuery(id+"F0.wireOp",EDGE,"E19.2.27")])]});
            var Q59;
            Q59=makeQuery(id+"F1.opExtrude","SWEPT_EDGE",EDGE,{"disambiguationData":[OSD([sQuery(id+"F0.wireOp",EDGE,"E19.2.1"),sQuery(id+"F0.wireOp",EDGE,"E19.2.19")])]});
            fillet(context, id + "F3", {"entities" : qUnion([Q0, Q1, Q2, Q3, Q4, Q5, Q6, Q7, Q8, Q9, Q10, Q11, Q12, Q13, Q14, Q15, Q16, Q17, Q18, Q19, Q20, Q21, Q22, Q23, Q24, Q25, Q26, Q27, Q28, Q29, Q30, Q31, Q32, Q33, Q34, Q35, Q36, Q37, Q38, Q39, Q40, Q41, Q42, Q43, Q44, Q45, Q46, Q47, Q48, Q49, Q50, Q51, Q52, Q53, Q54, Q55, Q56, Q57, Q58, Q59]), "tangentPropagation" : true, "radius" : .5 * mm, "defaultsChanged" : false, "vertexSettings" : [], "allowEdgeOverflow" : false});
        }
        {
            var Q0;
            Q0=makeQuery(id+"F1.opExtrude","SWEPT_EDGE",EDGE,{"disambiguationData":[OSD([sQuery(id+"F0.wireOp",EDGE,"E19.1.2"),sQuery(id+"F0.wireOp",EDGE,"E19.1.24")])]});
            var Q1;
            Q1=makeQuery(id+"F1.opExtrude","SWEPT_EDGE",EDGE,{"disambiguationData":[OSD([sQuery(id+"F0.wireOp",EDGE,"E19.1.13"),sQuery(id+"F0.wireOp",EDGE,"E19.1.25")])]});
            var Q2;
            Q2=makeQuery(id+"F1.opExtrude","SWEPT_EDGE",EDGE,{"disambiguationData":[OSD([sQuery(id+"F0.wireOp",EDGE,"E0.top"),sQuery(id+"F0.wireOp",EDGE,"E2.left")])]});
            var Q3;
            Q3=makeQuery(id+"F1.opExtrude","SWEPT_EDGE",EDGE,{"disambiguationData":[OSD([sQuery(id+"F0.wireOp",EDGE,"E2.right"),sQuery(id+"F0.wireOp",EDGE,"E7.trimOffspring")])]});
            var Q4;
            Q4=makeQuery(id+"F1.opExtrude","SWEPT_EDGE",EDGE,{"disambiguationData":[OSD([sQuery(id+"F0.wireOp",EDGE,"E19.5.13"),sQuery(id+"F0.wireOp",EDGE,"E19.5.25")])]});
            var Q5;
            Q5=makeQuery(id+"F1.opExtrude","SWEPT_EDGE",EDGE,{"disambiguationData":[OSD([sQuery(id+"F0.wireOp",EDGE,"E19.5.2"),sQuery(id+"F0.wireOp",EDGE,"E19.5.24")])]});
            var Q6;
            Q6=makeQuery(id+"F1.opExtrude","SWEPT_EDGE",EDGE,{"disambiguationData":[OSD([sQuery(id+"F0.wireOp",EDGE,"E19.4.13"),sQuery(id+"F0.wireOp",EDGE,"E19.4.25")])]});
            var Q7;
            Q7=makeQuery(id+"F1.opExtrude","SWEPT_EDGE",EDGE,{"disambiguationData":[OSD([sQuery(id+"F0.wireOp",EDGE,"E19.4.2"),sQuery(id+"F0.wireOp",EDGE,"E19.4.24")])]});
            var Q8;
            Q8=makeQuery(id+"F1.opExtrude","SWEPT_EDGE",EDGE,{"disambiguationData":[OSD([sQuery(id+"F0.wireOp",EDGE,"E19.3.13"),sQuery(id+"F0.wireOp",EDGE,"E19.3.25")])]});
            var Q9;
            Q9=makeQuery(id+"F1.opExtrude","SWEPT_EDGE",EDGE,{"disambiguationData":[OSD([sQuery(id+"F0.wireOp",EDGE,"E19.3.2"),sQuery(id+"F0.wireOp",EDGE,"E19.3.24")])]});
            var Q10;
            Q10=makeQuery(id+"F1.opExtrude","SWEPT_EDGE",EDGE,{"disambiguationData":[OSD([sQuery(id+"F0.wireOp",EDGE,"E19.2.13"),sQuery(id+"F0.wireOp",EDGE,"E19.2.25")])]});
            var Q11;
            Q11=makeQuery(id+"F1.opExtrude","SWEPT_EDGE",EDGE,{"disambiguationData":[OSD([sQuery(id+"F0.wireOp",EDGE,"E19.2.2"),sQuery(id+"F0.wireOp",EDGE,"E19.2.24")])]});
            fillet(context, id + "F4", {"entities" : qUnion([Q0, Q1, Q2, Q3, Q4, Q5, Q6, Q7, Q8, Q9, Q10, Q11]), "tangentPropagation" : true, "radius" : .5 * mm, "defaultsChanged" : false, "vertexSettings" : [], "allowEdgeOverflow" : false});
        }
        {
            var Q0;
            Q0=makeQuery(id+"F1.opExtrude","SWEPT_EDGE",EDGE,{"disambiguationData":[OSD([sQuery(id+"F0.wireOp",EDGE,"E19.1.30"),sQuery(id+"F0.wireOp",EDGE,"E22.trimOffspring")])]});
            var Q1;
            Q1=makeQuery(id+"F1.opExtrude","SWEPT_EDGE",EDGE,{"disambiguationData":[OSD([sQuery(id+"F0.wireOp",EDGE,"E3"),sQuery(id+"F0.wireOp",EDGE,"E19.1.29")])]});
            var Q2;
            Q2=makeQuery(id+"F1.opExtrude","SWEPT_EDGE",EDGE,{"disambiguationData":[OSD([sQuery(id+"F0.wireOp",EDGE,"E19.2.29"),sQuery(id+"F0.wireOp",EDGE,"E22.trimOffspring")])]});
            var Q3;
            Q3=makeQuery(id+"F1.opExtrude","SWEPT_EDGE",EDGE,{"disambiguationData":[OSD([sQuery(id+"F0.wireOp",EDGE,"E19.2.30"),sQuery(id+"F0.wireOp",EDGE,"E24.trimOffspring")])]});
            var Q4;
            Q4=makeQuery(id+"F1.opExtrude","SWEPT_EDGE",EDGE,{"disambiguationData":[OSD([sQuery(id+"F0.wireOp",EDGE,"E19.3.29"),sQuery(id+"F0.wireOp",EDGE,"E24.trimOffspring")])]});
            var Q5;
            Q5=makeQuery(id+"F1.opExtrude","SWEPT_EDGE",EDGE,{"disambiguationData":[OSD([sQuery(id+"F0.wireOp",EDGE,"E19.3.30"),sQuery(id+"F0.wireOp",EDGE,"E23.trimOffspring")])]});
            var Q6;
            Q6=makeQuery(id+"F1.opExtrude","SWEPT_EDGE",EDGE,{"disambiguationData":[OSD([sQuery(id+"F0.wireOp",EDGE,"E19.4.29"),sQuery(id+"F0.wireOp",EDGE,"E23.trimOffspring")])]});
            var Q7;
            Q7=makeQuery(id+"F1.opExtrude","SWEPT_EDGE",EDGE,{"disambiguationData":[OSD([sQuery(id+"F0.wireOp",EDGE,"E19.4.30"),sQuery(id+"F0.wireOp",EDGE,"E21.trimOffspring")])]});
            var Q8;
            Q8=makeQuery(id+"F1.opExtrude","SWEPT_EDGE",EDGE,{"disambiguationData":[OSD([sQuery(id+"F0.wireOp",EDGE,"E19.5.29"),sQuery(id+"F0.wireOp",EDGE,"E21.trimOffspring")])]});
            var Q9;
            Q9=makeQuery(id+"F1.opExtrude","SWEPT_EDGE",EDGE,{"disambiguationData":[OSD([sQuery(id+"F0.wireOp",EDGE,"E19.5.30"),sQuery(id+"F0.wireOp",EDGE,"E20.trimOffspring")])]});
            var Q10;
            Q10=makeQuery(id+"F1.opExtrude","SWEPT_EDGE",EDGE,{"disambiguationData":[OSD([sQuery(id+"F0.wireOp",EDGE,"E17.trimOffspring"),sQuery(id+"F0.wireOp",EDGE,"E20.trimOffspring")])]});
            var Q11;
            Q11=makeQuery(id+"F1.opExtrude","SWEPT_EDGE",EDGE,{"disambiguationData":[OSD([sQuery(id+"F0.wireOp",EDGE,"E3"),sQuery(id+"F0.wireOp",EDGE,"E16.trimOffspring")])]});
            fillet(context, id + "F5", {"entities" : qUnion([Q0, Q1, Q2, Q3, Q4, Q5, Q6, Q7, Q8, Q9, Q10, Q11]), "tangentPropagation" : true, "radius" : .5 * mm, "defaultsChanged" : false, "vertexSettings" : [], "allowEdgeOverflow" : false});
        }
    });
